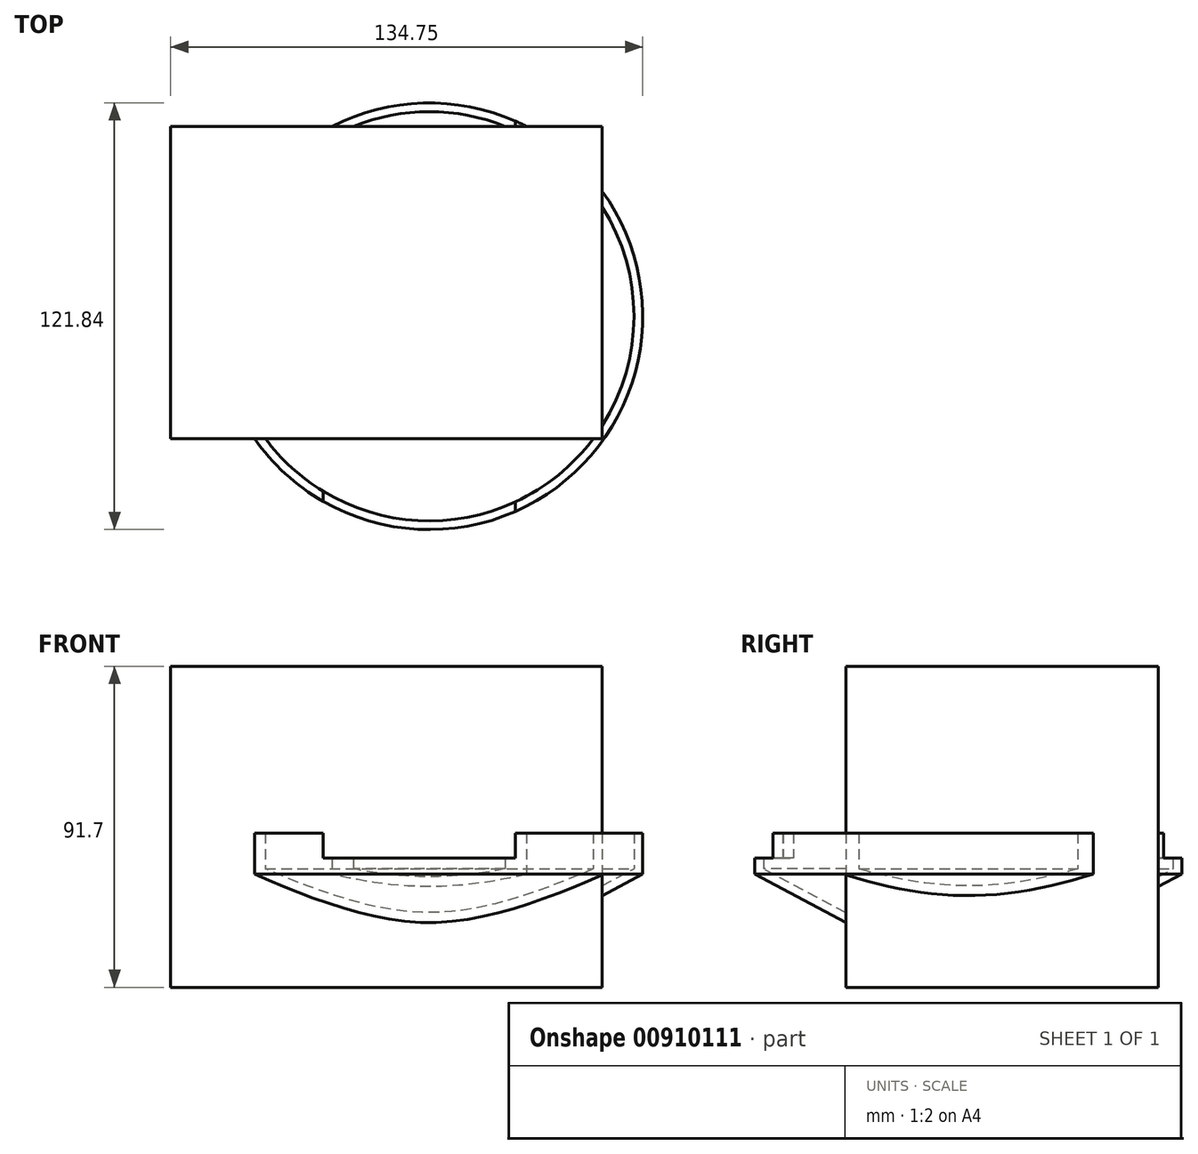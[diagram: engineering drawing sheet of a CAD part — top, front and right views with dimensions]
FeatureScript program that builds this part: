
annotation { "Feature Type Name" : "Feature", "Feature Type Description" : "" }
export const myFeature = defineFeature(function(context is Context, id is Id, definition is map)
    precondition{}
    {
        {
            var Q0;
            Q0=qCreatedBy(makeId("Front.planeOp"),FACE);
            var sketch = newSketch(context, id + "F0", { "sketchPlane" : qUnion([Q0])});
            skLineSegment(sketch, "E0", {"start": v(0, 0) * mm, "end": v(0, 44.08) * mm});
            skLineSegment(sketch, "E1", {"start": v(0, 44.08) * mm, "end": v(60.92, 44.08) * mm});
            skLineSegment(sketch, "E2", {"start": v(60.92, 44.08) * mm, "end": v(60.92, 32.3) * mm});
            skLineSegment(sketch, "E3", {"start": v(60.92, 32.3) * mm, "end": v(0, 0) * mm});
            skSolve(sketch);
        }
        {
            var Q0;
            Q0=makeQuery(id+"F0.imprint","IMPRINT",FACE,{"disambiguationData":[TD([[makeQuery(id+"F0.imprint","IMPRINT",EDGE,{"derivedFrom":sQuery(id+"F0.wireOp",EDGE,"E0")}),-1.0]])]});
            var Q1;
            Q1=sQuery(id+"F0.wireOp",EDGE,"E0");
            revolve(context, id + "F1", {"surfaceOperationType" : NewSurfaceOperationType.NEW, "entities" : qUnion([Q0]), "axis" : qUnion([Q1]), "revolveType" : RevolveType.FULL});
        }
        {
            var Q0;
            Q0=makeQuery(id+"F1.opRevolve","SWEPT_FACE",FACE,{"disambiguationData":[OSD([sQuery(id+"F0.wireOp",EDGE,"E1")])]});
            shell(context, id + "F2", {"entities" : qUnion([Q0]), "thickness" : 2.5 * mm});
        }
        {
            var Q0;
            Q0=qCreatedBy(makeId("Front.planeOp"),FACE);
            var sketch = newSketch(context, id + "F3", { "sketchPlane" : qUnion([Q0])});
            skLineSegment(sketch, "E4.bottom", {"start": v(-30.32, 53.46) * mm, "end": v(24.54, 53.46) * mm});
            skLineSegment(sketch, "E4.top", {"start": v(-30.32, 36.86) * mm, "end": v(24.54, 36.86) * mm});
            skLineSegment(sketch, "E4.left", {"start": v(-30.32, 53.46) * mm, "end": v(-30.32, 36.86) * mm});
            skLineSegment(sketch, "E4.right", {"start": v(24.54, 53.46) * mm, "end": v(24.54, 36.86) * mm});
            skSolve(sketch);
        }
        {
            var Q0;
            Q0=makeQuery(id+"F3.imprint","IMPRINT",FACE,{"disambiguationData":[TD([[makeQuery(id+"F3.imprint","IMPRINT",EDGE,{"derivedFrom":sQuery(id+"F3.wireOp",EDGE,"E4.bottom")}),-1.0]])]});
            extrude(context, id + "F4", {"entities" : qUnion([Q0]), "operationType" : NewBodyOperationType.REMOVE, "endBound" : BoundingType.SYMMETRIC, "oppositeDirection" : true, "depth" : 209 * mm, "offsetDistance" : 25 * mm});
        }
        {
            var Q0;
            Q0=qCreatedBy(makeId("Right.planeOp"),FACE);
            var sketch = newSketch(context, id + "F5", { "sketchPlane" : qUnion([Q0])});
            skLineSegment(sketch, "E5.bottom", {"start": v(35.74, -13.9) * mm, "end": v(-41.33, -13.9) * mm});
            skLineSegment(sketch, "E5.top", {"start": v(35.74, 10.36) * mm, "end": v(-41.33, 10.36) * mm});
            skLineSegment(sketch, "E5.left", {"start": v(35.74, -13.9) * mm, "end": v(35.74, 10.36) * mm});
            skLineSegment(sketch, "E5.right", {"start": v(-41.33, -13.9) * mm, "end": v(-41.33, 10.36) * mm});
            skSolve(sketch);
        }
        {
            var Q0;
            Q0=makeQuery(id+"F5.imprint","IMPRINT",FACE,{"disambiguationData":[TD([[makeQuery(id+"F5.imprint","IMPRINT",EDGE,{"derivedFrom":sQuery(id+"F5.wireOp",EDGE,"E5.bottom")}),-1.0]])]});
            extrude(context, id + "F6", {"entities" : qUnion([Q0]), "operationType" : NewBodyOperationType.REMOVE, "endBound" : BoundingType.SYMMETRIC, "oppositeDirection" : true, "depth" : 180.8 * mm, "offsetDistance" : 25 * mm});
        }
        {
            var Q0;
            Q0=qCreatedBy(makeId("Top.planeOp"),FACE);
            var sketch = newSketch(context, id + "F7", { "sketchPlane" : qUnion([Q0])});
            skLineSegment(sketch, "E6.bottom", {"start": v(-73.83, -34.9) * mm, "end": v(49.36, -34.9) * mm});
            skLineSegment(sketch, "E6.top", {"start": v(-73.83, 54.25) * mm, "end": v(49.36, 54.25) * mm});
            skLineSegment(sketch, "E6.left", {"start": v(-73.83, -34.9) * mm, "end": v(-73.83, 54.25) * mm});
            skLineSegment(sketch, "E6.right", {"start": v(49.36, -34.9) * mm, "end": v(49.36, 54.25) * mm});
            skPoint(sketch, "E6.middle", {"position": v(-12.24, 9.67) * mm});
            skSolve(sketch);
        }
        {
            var Q0;
            Q0=makeQuery(id+"F7.imprint","IMPRINT",FACE,{"disambiguationData":[TD([[makeQuery(id+"F7.imprint","IMPRINT",EDGE,{"derivedFrom":sQuery(id+"F7.wireOp",EDGE,"E6.bottom")}),1.0]])]});
            var sketch = newSketch(context, id + "F8", { "sketchPlane" : qUnion([Q0])});
            skSolve(sketch);
        }
        {
            var Q0;
            Q0=makeQuery(id+"F8.imprint","IMPRINT",FACE,{"disambiguationData":[TD([[makeQuery(id+"F8.imprint","IMPRINT",EDGE,{"derivedFrom":makeQuery(id+"F7.imprint","IMPRINT",EDGE,{"derivedFrom":sQuery(id+"F7.wireOp",EDGE,"E6.bottom")})}),1.0]])]});
            extrude(context, id + "F9", {"entities" : qUnion([Q0]), "operationType" : NewBodyOperationType.ADD, "depth" : 91.7 * mm, "offsetDistance" : 25 * mm});
        }
    });
